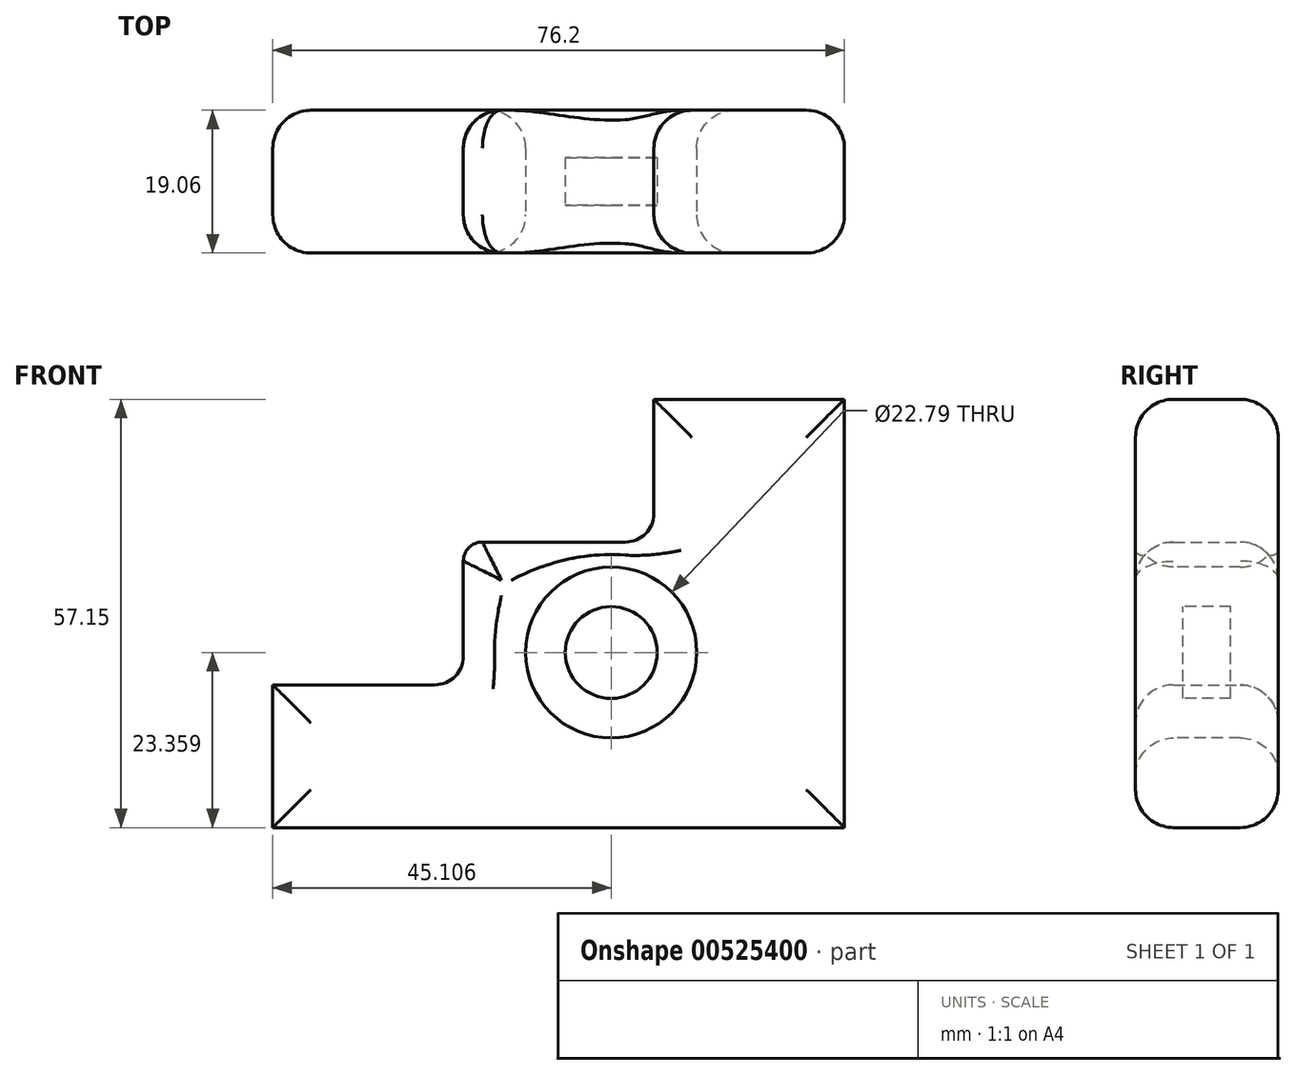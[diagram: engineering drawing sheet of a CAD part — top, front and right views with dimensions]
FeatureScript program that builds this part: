
annotation { "Feature Type Name" : "Feature", "Feature Type Description" : "" }
export const myFeature = defineFeature(function(context is Context, id is Id, definition is map)
    precondition{}
    {
        {
            var Q0;
            Q0=qCreatedBy(makeId("Front.planeOp"),FACE);
            var sketch = newSketch(context, id + "F0", { "sketchPlane" : qUnion([Q0])});
            skLineSegment(sketch, "E0", {"start": v(76.2, 0) * mm, "end": v(0, 0) * mm});
            skLineSegment(sketch, "E1", {"start": v(0, 0) * mm, "end": v(0, 19.05) * mm});
            skLineSegment(sketch, "E2", {"start": v(0, 19.05) * mm, "end": v(21.6, 19.05) * mm});
            skLineSegment(sketch, "E3", {"start": v(25.4, 22.86) * mm, "end": v(25.4, 35.56) * mm});
            skLineSegment(sketch, "E4", {"start": v(27.94, 38.1) * mm, "end": v(46.99, 38.1) * mm});
            skLineSegment(sketch, "E5", {"start": v(50.8, 41.91) * mm, "end": v(50.8, 57.15) * mm});
            skLineSegment(sketch, "E6", {"start": v(50.8, 57.15) * mm, "end": v(76.2, 57.15) * mm});
            skLineSegment(sketch, "E7", {"start": v(76.2, 57.15) * mm, "end": v(76.2, 0) * mm});
            skPoint(sketch, "E8.visualSharp", {"position": v(25.4, 19.05) * mm});
            skArc(sketch, "E8.filletArc", {"start": v(21.6, 19.05) * mm, "mid": v(24.28, 20.17) * mm, "end": v(25.4, 22.86) * mm});
            skPoint(sketch, "E9.visualSharp", {"position": v(50.8, 38.1) * mm});
            skArc(sketch, "E9.filletArc", {"start": v(46.99, 38.1) * mm, "mid": v(49.68, 39.22) * mm, "end": v(50.8, 41.91) * mm});
            skPoint(sketch, "E10.visualSharp", {"position": v(25.4, 38.1) * mm});
            skArc(sketch, "E10.filletArc", {"start": v(27.94, 38.1) * mm, "mid": v(26.14, 37.36) * mm, "end": v(25.4, 35.56) * mm});
            skSolve(sketch);
        }
        {
            var Q0;
            Q0 = qSketchRegion(id + "F0", true);
            extrude(context, id + "F1", {"entities" : qUnion([Q0]), "endBound" : BoundingType.SYMMETRIC, "depth" : 19.05 * mm, "offsetDistance" : 25.4 * mm});
        }
        {
            var Q0;
            Q0=makeQuery(id+"F1.opExtrude","CAP_FACE",FACE,{"disambiguationData":[OSD([sQuery(id+"F0.wireOp",EDGE,"E0"),sQuery(id+"F0.wireOp",EDGE,"E1"),sQuery(id+"F0.wireOp",EDGE,"E2"),sQuery(id+"F0.wireOp",EDGE,"E3"),sQuery(id+"F0.wireOp",EDGE,"E4"),sQuery(id+"F0.wireOp",EDGE,"E5"),sQuery(id+"F0.wireOp",EDGE,"E6"),sQuery(id+"F0.wireOp",EDGE,"E7"),sQuery(id+"F0.wireOp",EDGE,"E8.filletArc"),sQuery(id+"F0.wireOp",EDGE,"E9.filletArc"),sQuery(id+"F0.wireOp",EDGE,"E10.filletArc")])],"isStart":false});
            var sketch = newSketch(context, id + "F2", { "sketchPlane" : qUnion([Q0])});
            skCircle(sketch, "E11", {"center": v(45.1, 23.36) * mm, "radius": 11.4 * mm});
            skCircle(sketch, "E12", {"center": v(45.1, 23.36) * mm, "radius": 6.12 * mm});
            skSolve(sketch);
        }
        {
            var Q0;
            Q0=makeQuery(id+"F2.imprint","IMPRINT",FACE,{"disambiguationData":[TD([[makeQuery(id+"F2.imprint","IMPRINT",EDGE,{"derivedFrom":sQuery(id+"F2.wireOp",EDGE,"E11")}),1.0]])]});
            extrude(context, id + "F3", {"entities" : qUnion([Q0]), "operationType" : NewBodyOperationType.REMOVE, "oppositeDirection" : true, "depth" : 19.05 * mm, "offsetDistance" : 25.4 * mm});
        }
        {
            var Q0;
            Q0=makeQuery(id+"F3.boolean.opBoolean","SPLIT",FACE,{"disambiguationData":[TD([makeQuery(id+"F3.opExtrude","SWEPT_FACE",FACE,{"disambiguationData":[OSD([sQuery(id+"F2.wireOp",EDGE,"E12")])]})])],"derivedFrom":makeQuery(id+"F1.opExtrude","CAP_FACE",FACE,{"disambiguationData":[OSD([sQuery(id+"F0.wireOp",EDGE,"E0"),sQuery(id+"F0.wireOp",EDGE,"E1"),sQuery(id+"F0.wireOp",EDGE,"E2"),sQuery(id+"F0.wireOp",EDGE,"E3"),sQuery(id+"F0.wireOp",EDGE,"E4"),sQuery(id+"F0.wireOp",EDGE,"E5"),sQuery(id+"F0.wireOp",EDGE,"E6"),sQuery(id+"F0.wireOp",EDGE,"E7"),sQuery(id+"F0.wireOp",EDGE,"E8.filletArc"),sQuery(id+"F0.wireOp",EDGE,"E9.filletArc"),sQuery(id+"F0.wireOp",EDGE,"E10.filletArc")])],"isStart":true})});
            extrude(context, id + "F4", {"entities" : qUnion([Q0]), "operationType" : NewBodyOperationType.REMOVE, "oppositeDirection" : true, "depth" : 6.35 * mm, "offsetDistance" : 25.4 * mm});
        }
        {
            var Q0;
            Q0=makeQuery(id+"F3.boolean.opBoolean","SPLIT",FACE,{"disambiguationData":[TD([makeQuery(id+"F3.opExtrude","SWEPT_FACE",FACE,{"disambiguationData":[OSD([sQuery(id+"F2.wireOp",EDGE,"E12")])]})])],"derivedFrom":makeQuery(id+"F1.opExtrude","CAP_FACE",FACE,{"disambiguationData":[OSD([sQuery(id+"F0.wireOp",EDGE,"E0"),sQuery(id+"F0.wireOp",EDGE,"E1"),sQuery(id+"F0.wireOp",EDGE,"E2"),sQuery(id+"F0.wireOp",EDGE,"E3"),sQuery(id+"F0.wireOp",EDGE,"E4"),sQuery(id+"F0.wireOp",EDGE,"E5"),sQuery(id+"F0.wireOp",EDGE,"E6"),sQuery(id+"F0.wireOp",EDGE,"E7"),sQuery(id+"F0.wireOp",EDGE,"E8.filletArc"),sQuery(id+"F0.wireOp",EDGE,"E9.filletArc"),sQuery(id+"F0.wireOp",EDGE,"E10.filletArc")])],"isStart":false})});
            extrude(context, id + "F5", {"entities" : qUnion([Q0]), "operationType" : NewBodyOperationType.REMOVE, "oppositeDirection" : true, "depth" : 6.35 * mm, "offsetDistance" : 25.4 * mm});
        }
        {
            var Q0;
            {var subQ0=sQuery(id+"F0.wireOp",EDGE,"E8.filletArc");var subQ1=sQuery(id+"F0.wireOp",EDGE,"E7");var subQ2=sQuery(id+"F0.wireOp",EDGE,"E6");var subQ3=sQuery(id+"F0.wireOp",EDGE,"E5");var subQ4=sQuery(id+"F0.wireOp",EDGE,"E4");var subQ5=sQuery(id+"F0.wireOp",EDGE,"E9.filletArc");var subQ6=sQuery(id+"F0.wireOp",EDGE,"E0");var subQ7=sQuery(id+"F0.wireOp",EDGE,"E3");var subQ8=sQuery(id+"F0.wireOp",EDGE,"E1");var subQ9=sQuery(id+"F0.wireOp",EDGE,"E2");var subQ10=sQuery(id+"F0.wireOp",EDGE,"E10.filletArc");Q0=makeQuery(id+"F3.boolean.opBoolean","SPLIT",FACE,{"disambiguationData":[TD([makeQuery(id+"F1.opExtrude","SWEPT_FACE",FACE,{"disambiguationData":[OSD([subQ6])]})])],"derivedFrom":makeQuery(id+"F1.opExtrude","CAP_FACE",FACE,{"disambiguationData":[OSD([subQ6,subQ8,subQ9,subQ7,subQ4,subQ3,subQ2,subQ1,subQ0,subQ5,subQ10])],"isStart":false})});}
            var Q1;
            {var subQ0=sQuery(id+"F0.wireOp",EDGE,"E8.filletArc");var subQ1=sQuery(id+"F0.wireOp",EDGE,"E7");var subQ2=sQuery(id+"F0.wireOp",EDGE,"E6");var subQ3=sQuery(id+"F0.wireOp",EDGE,"E5");var subQ4=sQuery(id+"F0.wireOp",EDGE,"E4");var subQ5=sQuery(id+"F0.wireOp",EDGE,"E9.filletArc");var subQ6=sQuery(id+"F0.wireOp",EDGE,"E0");var subQ7=sQuery(id+"F0.wireOp",EDGE,"E3");var subQ8=sQuery(id+"F0.wireOp",EDGE,"E1");var subQ9=sQuery(id+"F0.wireOp",EDGE,"E2");var subQ10=sQuery(id+"F0.wireOp",EDGE,"E10.filletArc");Q1=makeQuery(id+"F3.boolean.opBoolean","SPLIT",FACE,{"disambiguationData":[TD([makeQuery(id+"F1.opExtrude","SWEPT_FACE",FACE,{"disambiguationData":[OSD([subQ6])]})])],"derivedFrom":makeQuery(id+"F1.opExtrude","CAP_FACE",FACE,{"disambiguationData":[OSD([subQ6,subQ8,subQ9,subQ7,subQ4,subQ3,subQ2,subQ1,subQ0,subQ5,subQ10])],"isStart":true})});}
            fillet(context, id + "F6", {"entities" : qUnion([Q0, Q1]), "radius" : 5.08 * mm, "tangentPropagation" : true, "allowEdgeOverflow" : false});
        }
    });
